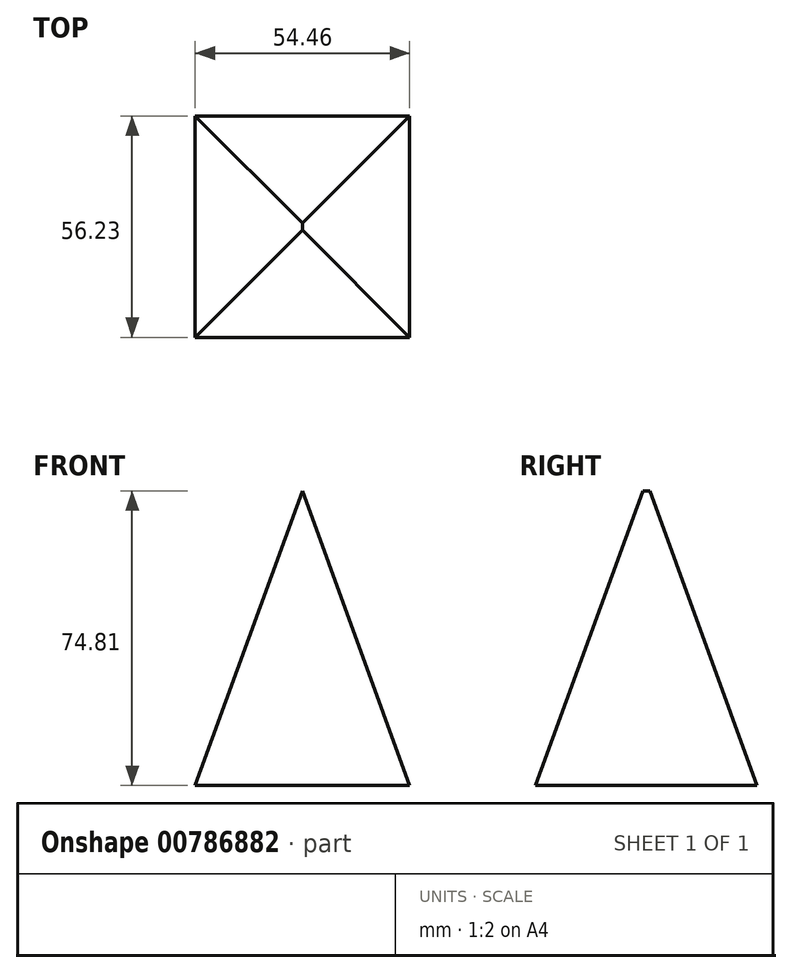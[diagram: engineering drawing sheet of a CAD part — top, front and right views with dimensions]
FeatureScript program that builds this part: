
annotation { "Feature Type Name" : "Feature", "Feature Type Description" : "" }
export const myFeature = defineFeature(function(context is Context, id is Id, definition is map)
    precondition{}
    {
        {
            var Q0;
            Q0=qCreatedBy(makeId("Top.planeOp"),FACE);
            var sketch = newSketch(context, id + "F0", { "sketchPlane" : qUnion([Q0])});
            skLineSegment(sketch, "E0.bottom", {"start": v(-27.82, -29.9) * mm, "end": v(26.64, -29.9) * mm});
            skLineSegment(sketch, "E0.top", {"start": v(-27.82, 26.34) * mm, "end": v(26.64, 26.34) * mm});
            skLineSegment(sketch, "E0.left", {"start": v(-27.82, -29.9) * mm, "end": v(-27.82, 26.34) * mm});
            skLineSegment(sketch, "E0.right", {"start": v(26.64, -29.9) * mm, "end": v(26.64, 26.34) * mm});
            skSolve(sketch);
        }
        {
            var Q0;
            Q0 = qSketchRegion(id + "F0", true);
            extrude(context, id + "F1", {"entities" : qUnion([Q0]), "depth" : 86.61 * mm, "offsetDistance" : 25.4 * mm, "hasDraft" : true, "draftAngle" : 20 * degree, "draftPullDirection" : true});
        }
    });
